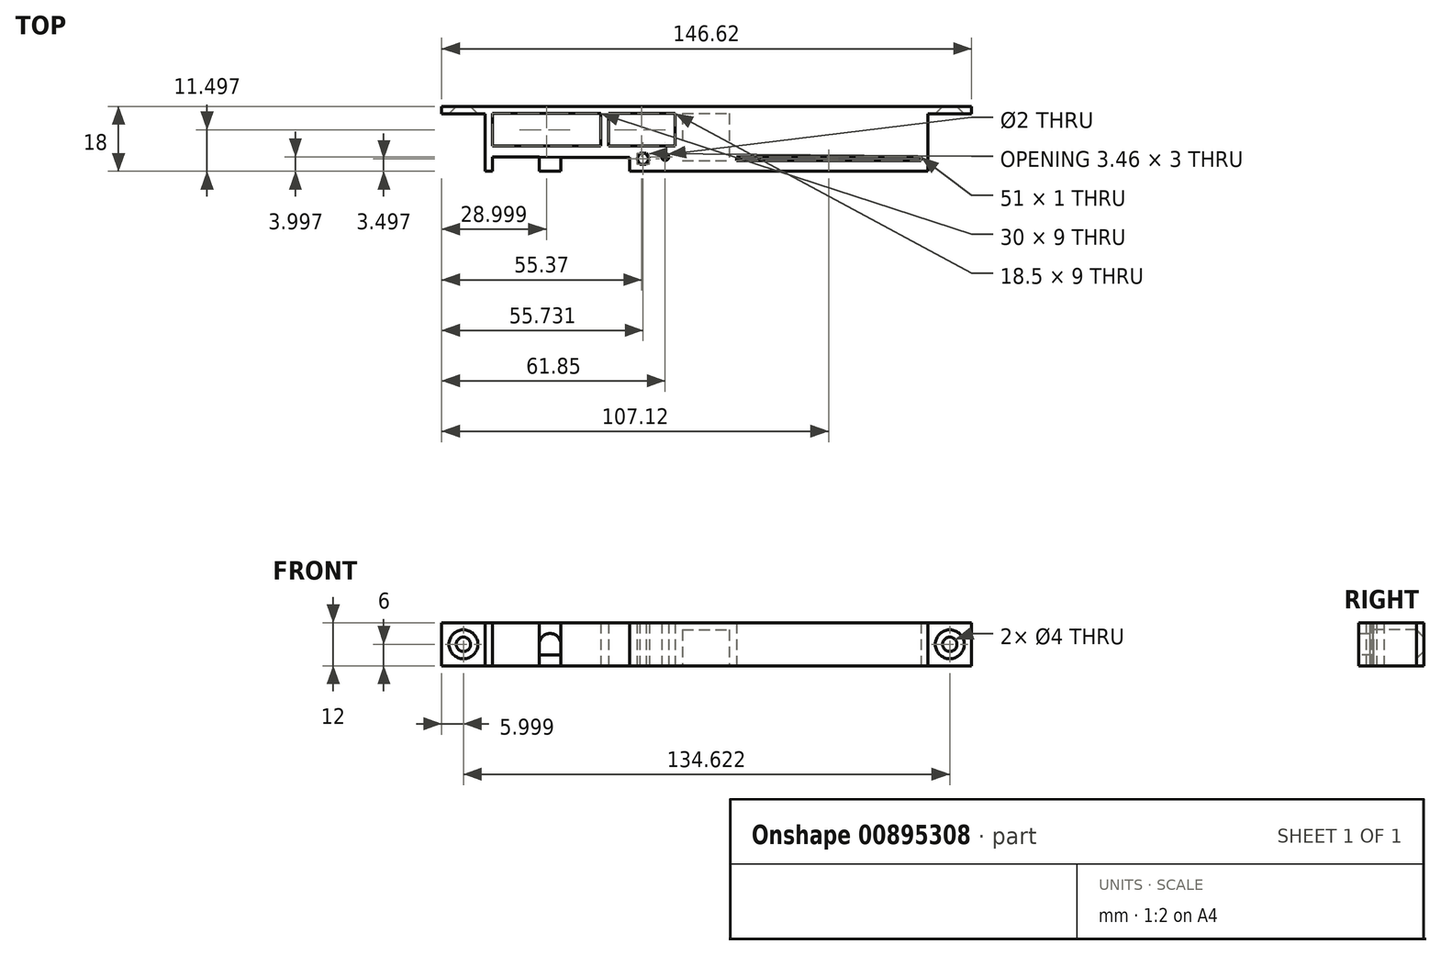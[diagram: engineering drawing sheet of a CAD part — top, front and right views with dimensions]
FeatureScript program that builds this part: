
annotation { "Feature Type Name" : "Feature", "Feature Type Description" : "" }
export const myFeature = defineFeature(function(context is Context, id is Id, definition is map)
    precondition{}
    {
        {
            var Q0;
            Q0=qCreatedBy(makeId("Top.planeOp"),FACE);
            var sketch = newSketch(context, id + "F0", { "sketchPlane" : qUnion([Q0])});
            skLineSegment(sketch, "E0.bottom", {"start": v(2.68, 9.12) * mm, "end": v(53.68, 9.12) * mm});
            skLineSegment(sketch, "E0.top", {"start": v(2.68, 8.12) * mm, "end": v(53.68, 8.12) * mm});
            skLineSegment(sketch, "E0.left", {"start": v(2.68, 9.12) * mm, "end": v(2.68, 8.12) * mm});
            skLineSegment(sketch, "E0.right", {"start": v(53.68, 9.12) * mm, "end": v(53.68, 8.12) * mm});
            skSolve(sketch);
        }
        {
            var Q0;
            Q0=qCreatedBy(makeId("Top.planeOp"),FACE);
            var sketch = newSketch(context, id + "F1", { "sketchPlane" : qUnion([Q0])});
            skLineSegment(sketch, "E1.bottom", {"start": v(-12.32, 21.12) * mm, "end": v(0.68, 21.12) * mm});
            skLineSegment(sketch, "E1.top", {"start": v(-12.32, 8.12) * mm, "end": v(0.68, 8.12) * mm});
            skLineSegment(sketch, "E1.left", {"start": v(-12.32, 21.12) * mm, "end": v(-12.32, 8.12) * mm});
            skLineSegment(sketch, "E1.right", {"start": v(0.68, 21.12) * mm, "end": v(0.68, 8.12) * mm});
            skSolve(sketch);
        }
        {
            var Q0;
            Q0=qCreatedBy(makeId("Top.planeOp"),FACE);
            var sketch = newSketch(context, id + "F2", { "sketchPlane" : qUnion([Q0])});
            skLineSegment(sketch, "E2.bottom", {"start": v(-64.94, 21.12) * mm, "end": v(-34.94, 21.12) * mm});
            skLineSegment(sketch, "E2.top", {"start": v(-64.94, 12.12) * mm, "end": v(-34.94, 12.12) * mm});
            skLineSegment(sketch, "E2.left", {"start": v(-64.94, 21.12) * mm, "end": v(-64.94, 12.12) * mm});
            skLineSegment(sketch, "E2.right", {"start": v(-34.94, 21.12) * mm, "end": v(-34.94, 12.12) * mm});
            skSolve(sketch);
        }
        {
            var Q0;
            Q0=qCreatedBy(makeId("Top.planeOp"),FACE);
            var sketch = newSketch(context, id + "F3", { "sketchPlane" : qUnion([Q0])});
            skLineSegment(sketch, "E3.bottom", {"start": v(-32.82, 21.12) * mm, "end": v(-14.32, 21.12) * mm});
            skLineSegment(sketch, "E3.top", {"start": v(-32.82, 12.12) * mm, "end": v(-14.32, 12.12) * mm});
            skLineSegment(sketch, "E3.left", {"start": v(-32.82, 21.12) * mm, "end": v(-32.82, 12.12) * mm});
            skLineSegment(sketch, "E3.right", {"start": v(-14.32, 21.12) * mm, "end": v(-14.32, 12.12) * mm});
            skSolve(sketch);
        }
        {
            var Q0;
            Q0=qCreatedBy(makeId("Top.planeOp"),FACE);
            var sketch = newSketch(context, id + "F4", { "sketchPlane" : qUnion([Q0])});
            skCircle(sketch, "E4.cCircle", {"center": v(-23.2, 8.62) * mm, "radius": 1.5 * mm, "construction": true});
            skLineSegment(sketch, "E4.0", {"start": v(-21.48, 8.62) * mm, "end": v(-22.34, 7.12) * mm});
            skLineSegment(sketch, "E4.1", {"start": v(-22.34, 7.12) * mm, "end": v(-24.08, 7.12) * mm});
            skLineSegment(sketch, "E4.2", {"start": v(-24.08, 7.12) * mm, "end": v(-24.94, 8.62) * mm});
            skLineSegment(sketch, "E4.3", {"start": v(-24.94, 8.62) * mm, "end": v(-24.08, 10.12) * mm});
            skLineSegment(sketch, "E4.4", {"start": v(-24.08, 10.12) * mm, "end": v(-22.34, 10.12) * mm});
            skLineSegment(sketch, "E4.5", {"start": v(-22.34, 10.12) * mm, "end": v(-21.48, 8.62) * mm});
            skPoint(sketch, "E4.0.midPoint", {"position": v(-21.91, 7.87) * mm});
            skSolve(sketch);
        }
        {
            var Q0;
            Q0=qCreatedBy(makeId("Top.planeOp"),FACE);
            var sketch = newSketch(context, id + "F5", { "sketchPlane" : qUnion([Q0])});
            skCircle(sketch, "E5", {"center": v(-17.09, 9.12) * mm, "radius": 1 * mm});
            skSolve(sketch);
        }
        {
            var Q0;
            Q0=qCreatedBy(makeId("Top.planeOp"),FACE);
            var sketch = newSketch(context, id + "F6", { "sketchPlane" : qUnion([Q0])});
            skLineSegment(sketch, "E6", {"start": v(-78.94, 23.12) * mm, "end": v(58.35, 23.12) * mm});
            skLineSegment(sketch, "E7", {"start": v(-78.94, 23.12) * mm, "end": v(-78.94, 21.07) * mm});
            skLineSegment(sketch, "E8", {"start": v(-78.94, 21.07) * mm, "end": v(-66.94, 21.07) * mm});
            skLineSegment(sketch, "E9", {"start": v(-66.94, 21.07) * mm, "end": v(-66.94, 5.12) * mm});
            skLineSegment(sketch, "E10", {"start": v(-66.94, 5.12) * mm, "end": v(55.68, 5.12) * mm});
            skLineSegment(sketch, "E11", {"start": v(55.68, 5.12) * mm, "end": v(55.68, 21.07) * mm});
            skLineSegment(sketch, "E12", {"start": v(55.68, 21.07) * mm, "end": v(67.68, 21.07) * mm});
            skLineSegment(sketch, "E13", {"start": v(67.68, 21.07) * mm, "end": v(67.68, 23.12) * mm});
            skLineSegment(sketch, "E14", {"start": v(67.68, 23.12) * mm, "end": v(58.35, 23.12) * mm});
            skLineSegment(sketch, "E15", {"start": v(-64.94, 5.12) * mm, "end": v(-64.94, 9.12) * mm});
            skLineSegment(sketch, "E16", {"start": v(-64.94, 9.12) * mm, "end": v(-51.94, 9.12) * mm});
            skLineSegment(sketch, "E17", {"start": v(-51.94, 9.12) * mm, "end": v(-51.94, 5.12) * mm});
            skLineSegment(sketch, "E18", {"start": v(-51.94, 5.12) * mm, "end": v(-26.94, 5.12) * mm});
            skLineSegment(sketch, "E19", {"start": v(-26.94, 5.12) * mm, "end": v(-26.94, 9) * mm});
            skLineSegment(sketch, "E20", {"start": v(-45.94, 9) * mm, "end": v(-26.94, 9) * mm});
            skLineSegment(sketch, "E21", {"start": v(-45.94, 9) * mm, "end": v(-45.94, 5.12) * mm});
            skLineSegment(sketch, "E22", {"start": v(-51.94, 9.12) * mm, "end": v(-45.94, 9) * mm});
            skSolve(sketch);
        }
        {
            var Q0;
            Q0=makeQuery(id+"F6.imprint","IMPRINT",FACE,{"disambiguationData":[TD([[makeQuery(id+"F6.imprint","IMPRINT",EDGE,{"derivedFrom":sQuery(id+"F6.wireOp",EDGE,"E6")}),-1.0]])]});
            extrude(context, id + "F7", {"entities" : qUnion([Q0]), "depth" : 12 * mm, "offsetDistance" : 25 * mm});
        }
        {
            var Q0;
            Q0=makeQuery(id+"F4.imprint","IMPRINT",FACE,{"disambiguationData":[TD([[makeQuery(id+"F4.imprint","IMPRINT",EDGE,{"derivedFrom":sQuery(id+"F4.wireOp",EDGE,"E4.0")}),-1.0]])]});
            var Q1;
            Q1=makeQuery(id+"F3.imprint","IMPRINT",FACE,{"disambiguationData":[TD([[makeQuery(id+"F3.imprint","IMPRINT",EDGE,{"derivedFrom":sQuery(id+"F3.wireOp",EDGE,"E3.bottom")}),-1.0]])]});
            var Q2;
            Q2=makeQuery(id+"F5.imprint","IMPRINT",FACE,{"disambiguationData":[TD([[makeQuery(id+"F5.imprint","IMPRINT",EDGE,{"derivedFrom":sQuery(id+"F5.wireOp",EDGE,"E5")}),1.0]])]});
            var Q3;
            Q3=makeQuery(id+"F2.imprint","IMPRINT",FACE,{"disambiguationData":[TD([[makeQuery(id+"F2.imprint","IMPRINT",EDGE,{"derivedFrom":sQuery(id+"F2.wireOp",EDGE,"E2.bottom")}),-1.0]])]});
            var Q4;
            Q4=makeQuery(id+"F0.imprint","IMPRINT",FACE,{"disambiguationData":[TD([[makeQuery(id+"F0.imprint","IMPRINT",EDGE,{"derivedFrom":sQuery(id+"F0.wireOp",EDGE,"E0.bottom")}),-1.0]])]});
            extrude(context, id + "F8", {"entities" : qUnion([Q0, Q1, Q2, Q3, Q4]), "operationType" : NewBodyOperationType.REMOVE, "depth" : 12 * mm, "offsetDistance" : 25 * mm});
        }
        {
            var Q0;
            {var subQ0=sQuery(id+"F6.wireOp",EDGE,"E17");Q0=makeQuery(id+"F6.imprint","IMPRINT",FACE,{"disambiguationData":[TD([[makeQuery(id+"F6.imprint","IMPRINT",EDGE,{"derivedFrom":subQ0}),1.0]])]});}
            extrude(context, id + "F9", {"entities" : qUnion([Q0]), "operationType" : NewBodyOperationType.ADD, "depth" : 9 * mm, "offsetDistance" : 25 * mm});
        }
        {
            var Q0;
            {var subQ0=sQuery(id+"F6.wireOp",EDGE,"E17");Q0=makeQuery(id+"F6.imprint","IMPRINT",FACE,{"disambiguationData":[TD([[makeQuery(id+"F6.imprint","IMPRINT",EDGE,{"derivedFrom":subQ0}),1.0]])]});}
            extrude(context, id + "F10", {"entities" : qUnion([Q0]), "operationType" : NewBodyOperationType.REMOVE, "depth" : 3 * mm, "offsetDistance" : 25 * mm});
        }
        {
            var Q0;
            Q0=makeQuery(id+"F9.opExtrude","CAP_EDGE",EDGE,{"disambiguationData":[OSD([sQuery(id+"F6.wireOp",EDGE,"E17")])],"isStart":false});
            var Q1;
            Q1=makeQuery(id+"F9.opExtrude","CAP_EDGE",EDGE,{"disambiguationData":[OSD([sQuery(id+"F6.wireOp",EDGE,"E21")])],"isStart":false});
            var Q2;
            Q2=makeQuery(id+"F10.boolean.opBoolean","COPY",EDGE,{"derivedFrom":makeQuery(id+"F10.opExtrude","CAP_EDGE",EDGE,{"disambiguationData":[OSD([sQuery(id+"F6.wireOp",EDGE,"E17")])],"isStart":false})});
            var Q3;
            Q3=makeQuery(id+"F10.boolean.opBoolean","COPY",EDGE,{"derivedFrom":makeQuery(id+"F10.opExtrude","CAP_EDGE",EDGE,{"disambiguationData":[OSD([sQuery(id+"F6.wireOp",EDGE,"E21")])],"isStart":false})});
            fillet(context, id + "F11", {"entities" : qUnion([Q0, Q1, Q2, Q3]), "radius" : 3 * mm, "tangentPropagation" : true, "allowEdgeOverflow" : false});
        }
        {
            var Q0;
            Q0=qCreatedBy(makeId("Front.planeOp"),FACE);
            var sketch = newSketch(context, id + "F12", { "sketchPlane" : qUnion([Q0])});
            skCircle(sketch, "E23", {"center": v(61.68, 6) * mm, "radius": 2 * mm});
            skSolve(sketch);
        }
        {
            var Q0;
            Q0=qCreatedBy(makeId("Front.planeOp"),FACE);
            var sketch = newSketch(context, id + "F13", { "sketchPlane" : qUnion([Q0])});
            skCircle(sketch, "E24", {"center": v(-72.94, 6) * mm, "radius": 2 * mm});
            skSolve(sketch);
        }
        {
            var Q0;
            Q0 = qSketchRegion(id + "F13", true);
            var Q1;
            Q1=makeQuery(id+"F12.imprint","IMPRINT",FACE,{"disambiguationData":[TD([[makeQuery(id+"F12.imprint","IMPRINT",EDGE,{"derivedFrom":sQuery(id+"F12.wireOp",EDGE,"E23")}),1.0]])]});
            extrude(context, id + "F14", {"entities" : qUnion([Q0, Q1]), "operationType" : NewBodyOperationType.REMOVE, "oppositeDirection" : true, "depth" : 23.9 * mm, "offsetDistance" : 25 * mm});
        }
        {
            var Q0;
            Q0=makeQuery(id+"F14.boolean.opBoolean","INTERSECT",EDGE,{"derivedFrom":[makeQuery(id+"F7.opExtrude","SWEPT_FACE",FACE,{"disambiguationData":[OSD([sQuery(id+"F6.wireOp",EDGE,"E8")])]}),makeQuery(id+"F14.opExtrude","SWEPT_FACE",FACE,{"disambiguationData":[OSD([sQuery(id+"F13.wireOp",EDGE,"E24")])]})]});
            var Q1;
            Q1=makeQuery(id+"F14.boolean.opBoolean","INTERSECT",EDGE,{"derivedFrom":[makeQuery(id+"F7.opExtrude","SWEPT_FACE",FACE,{"disambiguationData":[OSD([sQuery(id+"F6.wireOp",EDGE,"E12")])]}),makeQuery(id+"F14.opExtrude","SWEPT_FACE",FACE,{"disambiguationData":[OSD([sQuery(id+"F12.wireOp",EDGE,"E23")])]})]});
            chamfer(context, id + "F15", {"entities" : qUnion([Q0, Q1]), "width" : 2 * mm, "tangentPropagation" : true});
        }
        {
            var Q0;
            Q0=makeQuery(id+"F1.imprint","IMPRINT",FACE,{"disambiguationData":[TD([[makeQuery(id+"F1.imprint","IMPRINT",EDGE,{"derivedFrom":sQuery(id+"F1.wireOp",EDGE,"E1.bottom")}),-1.0]])]});
            extrude(context, id + "F16", {"entities" : qUnion([Q0]), "operationType" : NewBodyOperationType.REMOVE, "depth" : 10 * mm, "offsetDistance" : 25 * mm});
        }
    });
